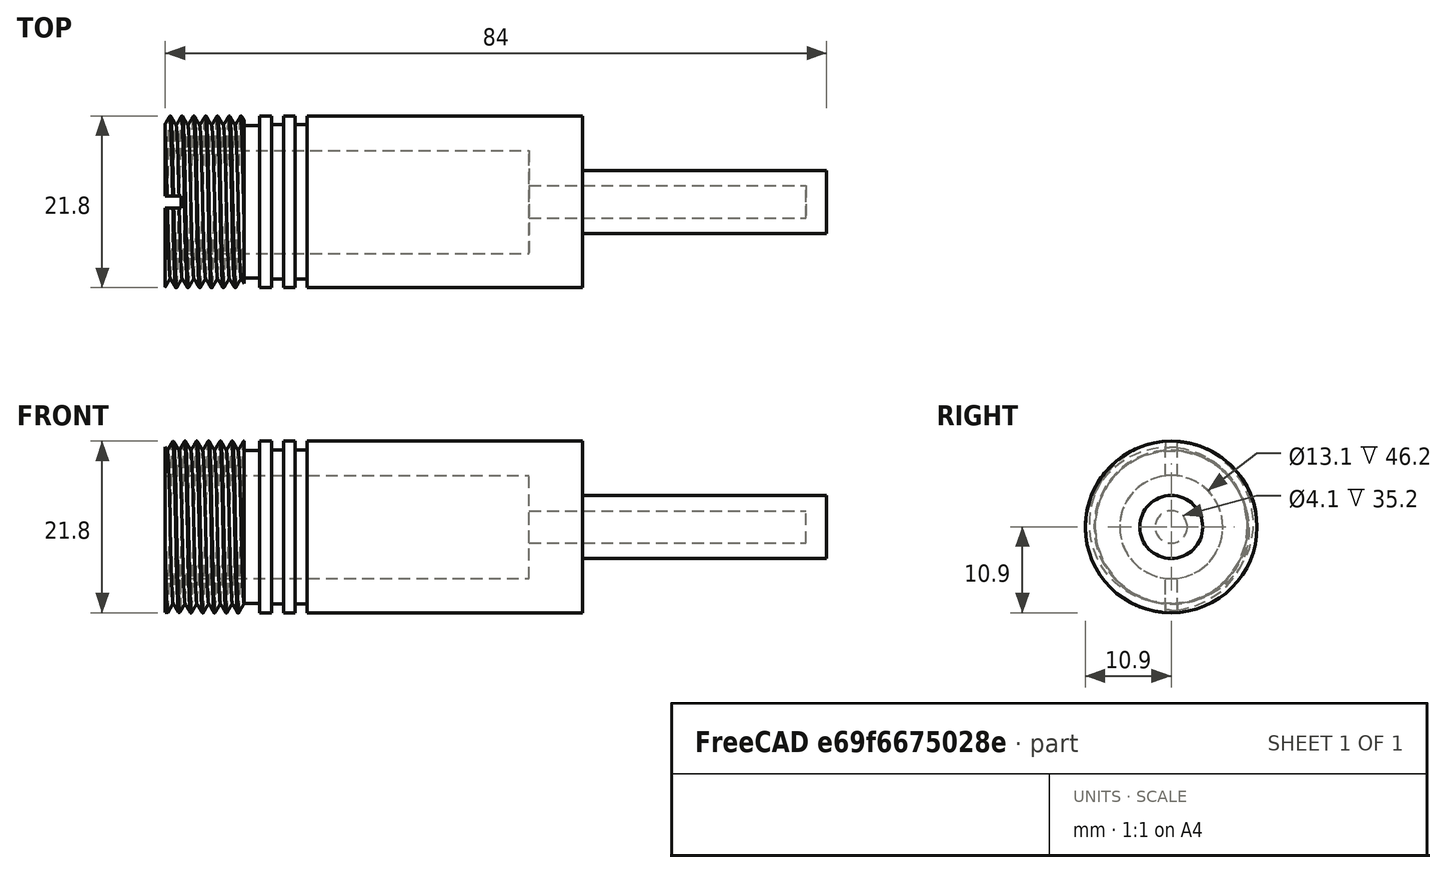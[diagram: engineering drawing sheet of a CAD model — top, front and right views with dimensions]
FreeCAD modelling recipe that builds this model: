
FCSTD DOCUMENT  (FreeCAD 0.17R13541 (Git))
Label: ERG-T-04-SH-01
License: All rights reserved
LicenseURL: http://en.wikipedia.org/wiki/All_rights_reserved
objects: Drawing::FeatureViewPython×17, Part::Cylinder×16, Part::Cut×11, Part::MultiFuse×4, Part::Helix×1, Sketcher::SketchObject×1, Part::Sweep×1, Part::Box×1, Drawing::FeatureViewPart×1, Drawing::FeaturePage×1
note: 35 computed .brp shape members not serialized (recipe doc carries the construction recipe); baked Part::Feature solids carry a one-line shape summary decoded from their .brp

FEATURE [Part::Cylinder] Cylinder072  label="Cylinder077"
  Angle = 360
  AttacherType = Attacher::AttachEngine3D
  Height = 18
  Placement = pos=(180.5,0,0) rot=(0,1,0;1.5708rad)
  Radius = 10.9
FEATURE [Part::Cylinder] Cylinder074  label="Cylinder083"
  Angle = 360
  AttacherType = Attacher::AttachEngine3D
  Height = 46.2
  Placement = pos=(180.5,0,0) rot=(0,1,0;1.5708rad)
  Radius = 6.55
FEATURE [Part::Cylinder] Cylinder075  label="Cylinder084"
  Angle = 360
  AttacherType = Attacher::AttachEngine3D
  Height = 53
  Placement = pos=(180.5,0,0) rot=(0,1,0;1.5708rad)
  Radius = 12.5
FEATURE [Part::Cylinder] Cylinder076  label="Cylinder085"
  Angle = 360
  AttacherType = Attacher::AttachEngine3D
  Height = 18
  Placement = pos=(180.5,0,0) rot=(0,1,0;1.5708rad)
  Radius = 12.5
FEATURE [Part::Cylinder] Cylinder077  label="Cylinder086"
  Angle = 360
  AttacherType = Attacher::AttachEngine3D
  Height = 31
  Placement = pos=(233.5,0,0) rot=(0,1,0;1.5708rad)
  Radius = 4
FEATURE [Part::Cut] Cut065
  Base = -> Cylinder076
  Tool = -> Cylinder072
FEATURE [Part::Cylinder] Cylinder080  label="Cylinder089"
  Angle = 360
  AttacherType = Attacher::AttachEngine3D
  Height = 35.2
  Placement = pos=(226.7,0,0) rot=(0,1,0;1.5708rad)
  Radius = 2.05
FEATURE [Part::MultiFuse] Fusion017  label="cavity"
  Shapes = -> [Cylinder080,Cylinder074]
FEATURE [Part::Helix] Helix019
  Angle = 0
  AttacherType = Attacher::AttachEngine3D
  Height = 17
  LocalCoord = 0
  Pitch = 1.5
  Placement = pos=(157,0,0) rot=(0,1,0;1.5708rad)
  Radius = 10.5
  Style = 1
FEATURE [Sketcher::SketchObject] Sketch023  label="T022"
  Placement = pos=(157,0,-11.01) rot=(1,0,0;1.5708rad)
  sketch-geometry (3):
    g0: LineSegment StartX=0 StartY=1.29904 StartZ=0 EndX=-0.75 EndY=0 EndZ=0
    g1: LineSegment StartX=0.75 StartY=0 StartZ=0 EndX=0 EndY=1.29904 EndZ=0
    g2: LineSegment StartX=-0.75 StartY=0 StartZ=0 EndX=0.75 EndY=0 EndZ=0
  constraints (9):
    c: PointOnObject(g1,g-1)
    c: Coincident(g1,g0)
    c: Coincident(g2,g0)
    c: Coincident(g2,g1)
    c: Horizontal(g2)
    c: Symmetric(g0,g1,g-2)
    c: Distance(g0,g1) = 1.5
    c: Angle(g1,g2) = 1.0472
    c: Angle(g2,g0) = 1.0472
FEATURE [Part::Sweep] Sweep016
  Frenet = true
  Sections = -> [Sketch023]
  Solid = true
  Spine = -> Helix019
  Transition = 1
FEATURE [Part::Cylinder] Cylinder084  label="Cylinder092"
  Angle = 360
  AttacherType = Attacher::AttachEngine3D
  Height = 1.5
  Placement = pos=(178,0,0) rot=(0,1,0;1.5708rad)
  Radius = 11
FEATURE [Part::Cylinder] Cylinder085  label="Cylinder093"
  Angle = 360
  AttacherType = Attacher::AttachEngine3D
  Height = 1.5
  Placement = pos=(178,0,0) rot=(0,1,0;1.5708rad)
  Radius = 9.8
FEATURE [Part::Cut] Cut071  label="circ2"
  Base = -> Cylinder084
  Placement = pos=(16,0,0) rot=(0,0,1;0rad)
  Tool = -> Cylinder085
FEATURE [Part::Cylinder] Cylinder086  label="Cylinder094"
  Angle = 360
  AttacherType = Attacher::AttachEngine3D
  Height = 2
  Placement = pos=(178,0,0) rot=(0,1,0;1.5708rad)
  Radius = 11
FEATURE [Part::Cylinder] Cylinder087  label="Cylinder095"
  Angle = 360
  AttacherType = Attacher::AttachEngine3D
  Height = 2
  Placement = pos=(178,0,0) rot=(0,1,0;1.5708rad)
  Radius = 9.7
FEATURE [Part::Cut] Cut072  label="circ1"
  Base = -> Cylinder086
  Placement = pos=(12.5,0,0) rot=(0,0,1;0rad)
  Tool = -> Cylinder087
FEATURE [Part::Cylinder] Cylinder088  label="Cylinder096"
  Angle = 360
  AttacherType = Attacher::AttachEngine3D
  Height = 10
  Placement = pos=(178,0,0) rot=(0,1,0;1.5708rad)
  Radius = 9
FEATURE [Part::Cylinder] Cylinder089  label="Cylinder097"
  Angle = 360
  AttacherType = Attacher::AttachEngine3D
  Height = 10
  Placement = pos=(178,0,0) rot=(0,1,0;1.5708rad)
  Radius = 11.5
FEATURE [Part::Cut] Cut074
  Base = -> Cylinder089
  Placement = pos=(-10.5,0,0) rot=(0,0,1;0rad)
  Tool = -> Cylinder088
FEATURE [Part::Box] Box  label="Cube"
  AttacherType = Attacher::AttachEngine3D
  Height = 30
  Length = 2
  Placement = pos=(180.5,-0.75,-15) rot=(0,0,1;0rad)
  Width = 1.5
FEATURE [Part::Cylinder] Cylinder091  label="Cylinder099"
  Angle = 360
  AttacherType = Attacher::AttachEngine3D
  Height = 35
  Placement = pos=(198.5,0,0) rot=(0,1,0;1.5708rad)
  Radius = 12.5
FEATURE [Part::Cylinder] Cylinder092  label="Cylinder100"
  Angle = 360
  AttacherType = Attacher::AttachEngine3D
  Height = 35
  Placement = pos=(198.5,0,0) rot=(0,1,0;1.5708rad)
  Radius = 10.9
FEATURE [Part::Cut] Cut
  Base = -> Cylinder091
  Tool = -> Cylinder092
FEATURE [Part::Cylinder] Cylinder093  label="Cylinder101"
  Angle = 360
  AttacherType = Attacher::AttachEngine3D
  Height = 1.5
  Placement = pos=(178,0,0) rot=(0,1,0;1.5708rad)
  Radius = 11
FEATURE [Part::Cylinder] Cylinder094  label="Cylinder102"
  Angle = 360
  AttacherType = Attacher::AttachEngine3D
  Height = 1.5
  Placement = pos=(178,0,0) rot=(0,1,0;1.5708rad)
  Radius = 9.8
FEATURE [Part::Cut] Cut076  label="circ3"
  Base = -> Cylinder093
  Placement = pos=(19,0,0) rot=(0,0,1;0rad)
  Tool = -> Cylinder094
FEATURE [Part::MultiFuse] Fusion019
  Shapes = -> [Cut,Cut065]
FEATURE [Part::MultiFuse] Fusion020
  Shapes = -> [Cylinder075,Cylinder077]
FEATURE [Part::Cut] Cut077  label="body"
  Base = -> Fusion020
  Tool = -> Fusion019
FEATURE [Part::Cut] Cut078  label="thread"
  Base = -> Sweep016
  Placement = pos=(23,0,0) rot=(0,0,1;0rad)
  Tool = -> Cut074
FEATURE [Part::MultiFuse] Fusion021  label="cutstuff"
  Shapes = -> [Cut078,Cut076,Cut072,Cut071]
FEATURE [Part::Cut] Cut079  label="outside"
  Base = -> Cut077
  Tool = -> Fusion021
FEATURE [Part::Cut] Cut080  label="holder01"
  Base = -> Cut079
  Tool = -> Fusion017
FEATURE [Part::Cut] Cut081  label="HOLDER"
  Base = -> Cut080
  Tool = -> Box
FEATURE [Drawing::FeatureViewPart] Ortho  label="Ortho_0_0"
  Direction = (0,1,0)
  HiddenWidth = 0.15
  LineWidth = 0.35
  Rotation = 90
  Scale = 2.5
  ShowHiddenLines = true
  ShowSmoothLines = false
  Source = -> Cut081
  Tolerance = 0.05
  ViewResult = <blob: 32848 chars omitted>
  Visible = true
  X = -407.75
  Y = 73.1186
FEATURE [Drawing::FeatureViewPython] dim001  # drawing view (typed FeaturePython)
  Rotation = 0
  ViewResult = <g> \n  <line x1="247.000000" y1="67.993600" x2="243.013684" y2="67.993600" style="stroke:rgb(255,0,0);stroke-width:0.10" />\n<line x1="247.000000" y1="78.243600" x2="243.013684" y2="78.243600" style="stroke:rgb(255,0,0);stroke-width:0.10" />\n<line x1="244.013684" y1="67.993600" x2="244.013684" y2="78.243600" style="stroke:rgb(255,0,0);stroke-width:0.10" /> \n  <polygon points="244.013684,78.243600 244.513684,76.243600 244.013684,75.743600 243.513684,76.243600" style="fill:rgb(255,0,0);stroke:rgb(255,0,0);stroke-width:0" /><polygon points="244.013684,67.993600 243.513684,69.993600 244.013684,70.493600 244.513684,69.993600" style="fill:rgb(255,0,0);stroke:rgb(255,0,0);stroke-width:0" /> \n  <text x="242.013684" y="73.118600" font-family="inherit" font-size="3.6" fill="rgb(0,0,0)" text-anchor="middle" transform="rotate(-90.000000 242.013684,73.118600)" >4.1</text> </g>
  Visible = true
  X = 0
  Y = 0
  arrowL1 = 2
  arrowL2 = 0.5
  arrowW = 1
  arrow_scheme = 0
  autoPlaceOffset = 2
  autoPlaceText = true
  click1_x = 244.014
  click1_y = 78.2593
  click2_x = 244.014
  click2_y = 78.2593
  comma_decimal_place = false
  dimension_line_overshoot = 1
  gap_datum_points = 0
  halfDimension_linear = false
  lineColor = rgb(255,0,0)
  strokeWidth = 0.1
  textFormat_linear = %(value)3.3f
  textRenderer_color = rgb(0,0,0)
  textRenderer_family = inherit
  textRenderer_size = 3.6
  unit_custom_scale = 1
  unit_scheme = 0
FEATURE [Drawing::FeatureViewPython] dim002  # drawing view (typed FeaturePython)
  Rotation = 0
  ViewResult = <g> \n  <line x1="253.500000" y1="63.118600" x2="263.329431" y2="63.118600" style="stroke:rgb(255,0,0);stroke-width:0.10" />\n<line x1="253.500000" y1="83.118600" x2="263.329431" y2="83.118600" style="stroke:rgb(255,0,0);stroke-width:0.10" />\n<line x1="262.329431" y1="63.118600" x2="262.329431" y2="83.118600" style="stroke:rgb(255,0,0);stroke-width:0.10" /> \n  <polygon points="262.329431,83.118600 262.829431,81.118600 262.329431,80.618600 261.829431,81.118600" style="fill:rgb(255,0,0);stroke:rgb(255,0,0);stroke-width:0" /><polygon points="262.329431,63.118600 261.829431,65.118600 262.329431,65.618600 262.829431,65.118600" style="fill:rgb(255,0,0);stroke:rgb(255,0,0);stroke-width:0" /> \n  <text x="260.329431" y="73.118600" font-family="inherit" font-size="3.6" fill="rgb(0,0,0)" text-anchor="middle" transform="rotate(-90.000000 260.329431,73.118600)" >8</text> </g>
  Visible = true
  X = 0
  Y = 0
  arrowL1 = 2
  arrowL2 = 0.5
  arrowW = 1
  arrow_scheme = 0
  autoPlaceOffset = 2
  autoPlaceText = true
  click1_x = 262.329
  click1_y = 85.3497
  click2_x = 262.329
  click2_y = 85.3497
  comma_decimal_place = false
  dimension_line_overshoot = 1
  gap_datum_points = 0
  halfDimension_linear = false
  lineColor = rgb(255,0,0)
  strokeWidth = 0.1
  textFormat_linear = %(value)3.3f
  textRenderer_color = rgb(0,0,0)
  textRenderer_family = inherit
  textRenderer_size = 3.6
  unit_custom_scale = 1
  unit_scheme = 0
FEATURE [Drawing::FeatureViewPython] dim005  # drawing view (typed FeaturePython)
  Rotation = 0
  ViewResult = <g> \n  <line x1="88.500000" y1="45.868600" x2="88.500000" y2="32.082769" style="stroke:rgb(255,0,0);stroke-width:0.10" />\n<line x1="176.000000" y1="45.868600" x2="176.000000" y2="32.082769" style="stroke:rgb(255,0,0);stroke-width:0.10" />\n<line x1="88.500000" y1="33.082769" x2="176.000000" y2="33.082769" style="stroke:rgb(255,0,0);stroke-width:0.10" /> \n  <polygon points="176.000000,33.082769 174.000000,32.582769 173.500000,33.082769 174.000000,33.582769" style="fill:rgb(255,0,0);stroke:rgb(255,0,0);stroke-width:0" /><polygon points="88.500000,33.082769 90.500000,33.582769 91.000000,33.082769 90.500000,32.582769" style="fill:rgb(255,0,0);stroke:rgb(255,0,0);stroke-width:0" /> \n  <text x="132.250000" y="31.082769" font-family="inherit" font-size="3.6" fill="rgb(0,0,0)" text-anchor="middle" transform="rotate(0.000000 132.250000,31.082769)" >35</text> </g>
  Visible = true
  X = 0
  Y = 0
  arrowL1 = 2
  arrowL2 = 0.5
  arrowW = 1
  arrow_scheme = 0
  autoPlaceOffset = 2
  autoPlaceText = true
  click1_x = 161.182
  click1_y = 33.0828
  click2_x = 161.182
  click2_y = 33.0828
  comma_decimal_place = false
  dimension_line_overshoot = 1
  gap_datum_points = 0
  halfDimension_linear = false
  lineColor = rgb(255,0,0)
  strokeWidth = 0.1
  textFormat_linear = %(value)3.3f
  textRenderer_color = rgb(0,0,0)
  textRenderer_family = inherit
  textRenderer_size = 3.6
  unit_custom_scale = 1
  unit_scheme = 0
FEATURE [Drawing::FeatureViewPython] dim006  # drawing view (typed FeaturePython)
  Rotation = 0
  ViewResult = <g> \n  <line x1="88.500000" y1="45.868600" x2="88.500000" y2="32.094010" style="stroke:rgb(255,0,0);stroke-width:0.10" />\n<line x1="68.500000" y1="48.819225" x2="68.500000" y2="32.094010" style="stroke:rgb(255,0,0);stroke-width:0.10" />\n<line x1="88.500000" y1="33.094010" x2="68.500000" y2="33.094010" style="stroke:rgb(255,0,0);stroke-width:0.10" /> \n  <polygon points="68.500000,33.094010 70.500000,33.594010 71.000000,33.094010 70.500000,32.594010" style="fill:rgb(255,0,0);stroke:rgb(255,0,0);stroke-width:0" /><polygon points="88.500000,33.094010 86.500000,32.594010 86.000000,33.094010 86.500000,33.594010" style="fill:rgb(255,0,0);stroke:rgb(255,0,0);stroke-width:0" /> \n  <text x="78.500000" y="31.094010" font-family="inherit" font-size="3.6" fill="rgb(0,0,0)" text-anchor="middle" transform="rotate(0.000000 78.500000,31.094010)" >8</text> </g>
  Visible = true
  X = 0
  Y = 0
  arrowL1 = 2
  arrowL2 = 0.5
  arrowW = 1
  arrow_scheme = 0
  autoPlaceOffset = 2
  autoPlaceText = true
  click1_x = 69.9279
  click1_y = 33.094
  click2_x = 69.9279
  click2_y = 33.094
  comma_decimal_place = false
  dimension_line_overshoot = 1
  gap_datum_points = 0
  halfDimension_linear = false
  lineColor = rgb(255,0,0)
  strokeWidth = 0.1
  textFormat_linear = %(value)3.3f
  textRenderer_color = rgb(0,0,0)
  textRenderer_family = inherit
  textRenderer_size = 3.6
  unit_custom_scale = 1
  unit_scheme = 0
FEATURE [Drawing::FeatureViewPython] dim007  # drawing view (typed FeaturePython)
  Rotation = 0
  ViewResult = <g> \n  <line x1="68.500000" y1="48.819225" x2="68.500000" y2="32.164573" style="stroke:rgb(255,0,0);stroke-width:0.10" />\n<line x1="43.500000" y1="45.933100" x2="43.500000" y2="32.164573" style="stroke:rgb(255,0,0);stroke-width:0.10" />\n<line x1="68.500000" y1="33.164573" x2="43.500000" y2="33.164573" style="stroke:rgb(255,0,0);stroke-width:0.10" /> \n  <polygon points="43.500000,33.164573 45.500000,33.664573 46.000000,33.164573 45.500000,32.664573" style="fill:rgb(255,0,0);stroke:rgb(255,0,0);stroke-width:0" /><polygon points="68.500000,33.164573 66.500000,32.664573 66.000000,33.164573 66.500000,33.664573" style="fill:rgb(255,0,0);stroke:rgb(255,0,0);stroke-width:0" /> \n  <text x="56.000000" y="31.164573" font-family="inherit" font-size="3.6" fill="rgb(0,0,0)" text-anchor="middle" transform="rotate(0.000000 56.000000,31.164573)" >10</text> </g>
  Visible = true
  X = 0
  Y = 0
  arrowL1 = 2
  arrowL2 = 0.5
  arrowW = 1
  arrow_scheme = 0
  autoPlaceOffset = 2
  autoPlaceText = true
  click1_x = 44.5958
  click1_y = 33.1646
  click2_x = 44.5958
  click2_y = 33.1646
  comma_decimal_place = false
  dimension_line_overshoot = 1
  gap_datum_points = 0
  halfDimension_linear = false
  lineColor = rgb(255,0,0)
  strokeWidth = 0.1
  textFormat_linear = %(value)3.3f
  textRenderer_color = rgb(0,0,0)
  textRenderer_family = inherit
  textRenderer_size = 3.6
  unit_custom_scale = 1
  unit_scheme = 0
FEATURE [Drawing::FeatureViewPython] dim004  # drawing view (typed FeaturePython)
  Rotation = 0
  ViewResult = <g> \n  <line x1="176.000000" y1="63.118600" x2="176.000000" y2="32.081558" style="stroke:rgb(255,0,0);stroke-width:0.10" />\n<line x1="253.500000" y1="63.118600" x2="253.500000" y2="32.081558" style="stroke:rgb(255,0,0);stroke-width:0.10" />\n<line x1="176.000000" y1="33.081558" x2="253.500000" y2="33.081558" style="stroke:rgb(255,0,0);stroke-width:0.10" /> \n  <polygon points="253.500000,33.081558 251.500000,32.581558 251.000000,33.081558 251.500000,33.581558" style="fill:rgb(255,0,0);stroke:rgb(255,0,0);stroke-width:0" /><polygon points="176.000000,33.081558 178.000000,33.581558 178.500000,33.081558 178.000000,32.581558" style="fill:rgb(255,0,0);stroke:rgb(255,0,0);stroke-width:0" /> \n  <text x="214.750000" y="31.081558" font-family="inherit" font-size="3.6" fill="rgb(0,0,0)" text-anchor="middle" transform="rotate(0.000000 214.750000,31.081558)" >31</text> </g>
  Visible = true
  X = 0
  Y = 0
  arrowL1 = 2
  arrowL2 = 0.5
  arrowW = 1
  arrow_scheme = 0
  autoPlaceOffset = 2
  autoPlaceText = true
  click1_x = 187.265
  click1_y = 33.0816
  click2_x = 187.265
  click2_y = 33.0816
  comma_decimal_place = false
  dimension_line_overshoot = 1
  gap_datum_points = 0
  halfDimension_linear = false
  lineColor = rgb(255,0,0)
  strokeWidth = 0.1
  textFormat_linear = %(value)3.3f
  textRenderer_color = rgb(0,0,0)
  textRenderer_family = inherit
  textRenderer_size = 3.6
  unit_custom_scale = 1
  unit_scheme = 0
FEATURE [Drawing::FeatureViewPython] dim008  # drawing view (typed FeaturePython)
  Rotation = 0
  ViewResult = <g> \n  <line x1="159.000000" y1="56.743600" x2="150.188443" y2="56.743600" style="stroke:rgb(255,0,0);stroke-width:0.10" />\n<line x1="159.000000" y1="89.493600" x2="150.188443" y2="89.493600" style="stroke:rgb(255,0,0);stroke-width:0.10" />\n<line x1="151.188443" y1="56.743600" x2="151.188443" y2="89.493600" style="stroke:rgb(255,0,0);stroke-width:0.10" /> \n  <polygon points="151.188443,89.493600 151.688443,87.493600 151.188443,86.993600 150.688443,87.493600" style="fill:rgb(255,0,0);stroke:rgb(255,0,0);stroke-width:0" /><polygon points="151.188443,56.743600 150.688443,58.743600 151.188443,59.243600 151.688443,58.743600" style="fill:rgb(255,0,0);stroke:rgb(255,0,0);stroke-width:0" /> \n  <text x="149.188443" y="73.118600" font-family="inherit" font-size="3.6" fill="rgb(0,0,0)" text-anchor="middle" transform="rotate(-90.000000 149.188443,73.118600)" >13.1</text> </g>
  Visible = true
  X = 0
  Y = 0
  arrowL1 = 2
  arrowL2 = 0.5
  arrowW = 1
  arrow_scheme = 0
  autoPlaceOffset = 2
  autoPlaceText = true
  click1_x = 151.188
  click1_y = 89.0644
  click2_x = 151.188
  click2_y = 89.0644
  comma_decimal_place = false
  dimension_line_overshoot = 1
  gap_datum_points = 0
  halfDimension_linear = false
  lineColor = rgb(255,0,0)
  strokeWidth = 0.1
  textFormat_linear = %(value)3.3f
  textRenderer_color = rgb(0,0,0)
  textRenderer_family = inherit
  textRenderer_size = 3.6
  unit_custom_scale = 1
  unit_scheme = 0
FEATURE [Drawing::FeatureViewPython] dim009  # drawing view (typed FeaturePython)
  Rotation = 0
  ViewResult = <g> \n  <line x1="43.500000" y1="45.933100" x2="43.500000" y2="19.353229" style="stroke:rgb(255,0,0);stroke-width:0.10" />\n<line x1="253.500000" y1="63.118600" x2="253.500000" y2="19.353229" style="stroke:rgb(255,0,0);stroke-width:0.10" />\n<line x1="43.500000" y1="20.353229" x2="253.500000" y2="20.353229" style="stroke:rgb(255,0,0);stroke-width:0.10" /> \n  <polygon points="253.500000,20.353229 251.500000,19.853229 251.000000,20.353229 251.500000,20.853229" style="fill:rgb(255,0,0);stroke:rgb(255,0,0);stroke-width:0" /><polygon points="43.500000,20.353229 45.500000,20.853229 46.000000,20.353229 45.500000,19.853229" style="fill:rgb(255,0,0);stroke:rgb(255,0,0);stroke-width:0" /> \n  <text x="148.500000" y="18.353229" font-family="inherit" font-size="3.6" fill="rgb(0,0,0)" text-anchor="middle" transform="rotate(0.000000 148.500000,18.353229)" >84</text> </g>
  Visible = true
  X = 0
  Y = 0
  arrowL1 = 2
  arrowL2 = 0.5
  arrowW = 1
  arrow_scheme = 0
  autoPlaceOffset = 2
  autoPlaceText = true
  click1_x = 240.819
  click1_y = 20.3532
  click2_x = 240.819
  click2_y = 20.3532
  comma_decimal_place = false
  dimension_line_overshoot = 1
  gap_datum_points = 0
  halfDimension_linear = false
  lineColor = rgb(255,0,0)
  strokeWidth = 0.1
  textFormat_linear = %(value)3.3f
  textRenderer_color = rgb(0,0,0)
  textRenderer_family = inherit
  textRenderer_size = 3.6
  unit_custom_scale = 1
  unit_scheme = 0
FEATURE [Drawing::FeatureViewPython] dim010  # drawing view (typed FeaturePython)
  Rotation = 0
  ViewResult = <g> \n  <line x1="247.000000" y1="78.243600" x2="247.000000" y2="113.371059" style="stroke:rgb(255,0,0);stroke-width:0.10" />\n<line x1="159.000000" y1="89.493600" x2="159.000000" y2="113.371059" style="stroke:rgb(255,0,0);stroke-width:0.10" />\n<line x1="247.000000" y1="112.371059" x2="159.000000" y2="112.371059" style="stroke:rgb(255,0,0);stroke-width:0.10" /> \n  <polygon points="159.000000,112.371059 161.000000,112.871059 161.500000,112.371059 161.000000,111.871059" style="fill:rgb(255,0,0);stroke:rgb(255,0,0);stroke-width:0" /><polygon points="247.000000,112.371059 245.000000,111.871059 244.500000,112.371059 245.000000,112.871059" style="fill:rgb(255,0,0);stroke:rgb(255,0,0);stroke-width:0" /> \n  <text x="203.000000" y="110.371059" font-family="inherit" font-size="3.6" fill="rgb(0,0,0)" text-anchor="middle" transform="rotate(0.000000 203.000000,110.371059)" >35.2</text> </g>
  Visible = true
  X = 0
  Y = 0
  arrowL1 = 2
  arrowL2 = 0.5
  arrowW = 1
  arrow_scheme = 0
  autoPlaceOffset = 2
  autoPlaceText = true
  click1_x = 170.192
  click1_y = 112.371
  click2_x = 170.192
  click2_y = 112.371
  comma_decimal_place = false
  dimension_line_overshoot = 1
  gap_datum_points = 0
  halfDimension_linear = false
  lineColor = rgb(255,0,0)
  strokeWidth = 0.1
  textFormat_linear = %(value)3.3f
  textRenderer_color = rgb(0,0,0)
  textRenderer_family = inherit
  textRenderer_size = 3.6
  unit_custom_scale = 1
  unit_scheme = 0
FEATURE [Drawing::FeatureViewPython] dim011  # drawing view (typed FeaturePython)
  Rotation = 0
  ViewResult = <g> \n  <line x1="159.000000" y1="89.493600" x2="159.000000" y2="113.377984" style="stroke:rgb(255,0,0);stroke-width:0.10" />\n<line x1="43.500000" y1="98.332100" x2="43.500000" y2="113.377984" style="stroke:rgb(255,0,0);stroke-width:0.10" />\n<line x1="159.000000" y1="112.377984" x2="43.500000" y2="112.377984" style="stroke:rgb(255,0,0);stroke-width:0.10" /> \n  <polygon points="43.500000,112.377984 45.500000,112.877984 46.000000,112.377984 45.500000,111.877984" style="fill:rgb(255,0,0);stroke:rgb(255,0,0);stroke-width:0" /><polygon points="159.000000,112.377984 157.000000,111.877984 156.500000,112.377984 157.000000,112.877984" style="fill:rgb(255,0,0);stroke:rgb(255,0,0);stroke-width:0" /> \n  <text x="101.250000" y="110.377984" font-family="inherit" font-size="3.6" fill="rgb(0,0,0)" text-anchor="middle" transform="rotate(0.000000 101.250000,110.377984)" >46.2</text> </g>
  Visible = true
  X = 0
  Y = 0
  arrowL1 = 2
  arrowL2 = 0.5
  arrowW = 1
  arrow_scheme = 0
  autoPlaceOffset = 2
  autoPlaceText = true
  click1_x = 155.5
  click1_y = 112.378
  click2_x = 155.5
  click2_y = 112.378
  comma_decimal_place = false
  dimension_line_overshoot = 1
  gap_datum_points = 0
  halfDimension_linear = false
  lineColor = rgb(255,0,0)
  strokeWidth = 0.1
  textFormat_linear = %(value)3.3f
  textRenderer_color = rgb(0,0,0)
  textRenderer_family = inherit
  textRenderer_size = 3.6
  unit_custom_scale = 1
  unit_scheme = 0
FEATURE [Drawing::FeatureViewPython] dim013  # drawing view (typed FeaturePython)
  Rotation = 0
  ViewResult = <g> \n  <line x1="88.500000" y1="48.618600" x2="96.671560" y2="48.618600" style="stroke:rgb(255,0,0);stroke-width:0.10" />\n<line x1="88.500000" y1="97.618600" x2="96.671560" y2="97.618600" style="stroke:rgb(255,0,0);stroke-width:0.10" />\n<line x1="95.671560" y1="48.618600" x2="95.671560" y2="97.618600" style="stroke:rgb(255,0,0);stroke-width:0.10" /> \n  <polygon points="95.671560,97.618600 96.171560,95.618600 95.671560,95.118600 95.171560,95.618600" style="fill:rgb(255,0,0);stroke:rgb(255,0,0);stroke-width:0" /><polygon points="95.671560,48.618600 95.171560,50.618600 95.671560,51.118600 96.171560,50.618600" style="fill:rgb(255,0,0);stroke:rgb(255,0,0);stroke-width:0" /> \n  <text x="93.671560" y="73.118600" font-family="inherit" font-size="3.6" fill="rgb(0,0,0)" text-anchor="middle" transform="rotate(-90.000000 93.671560,73.118600)" >19.6</text> </g>
  Visible = true
  X = 0
  Y = 0
  arrowL1 = 2
  arrowL2 = 0.5
  arrowW = 1
  arrow_scheme = 0
  autoPlaceOffset = 2
  autoPlaceText = true
  click1_x = 95.6716
  click1_y = 97.5532
  click2_x = 95.6716
  click2_y = 97.5532
  comma_decimal_place = false
  dimension_line_overshoot = 1
  gap_datum_points = 0
  halfDimension_linear = false
  lineColor = rgb(255,0,0)
  strokeWidth = 0.1
  textFormat_linear = %(value)3.3f
  textRenderer_color = rgb(0,0,0)
  textRenderer_family = inherit
  textRenderer_size = 3.6
  unit_custom_scale = 1
  unit_scheme = 0
FEATURE [Drawing::FeatureViewPython] dim003  # drawing view (typed FeaturePython)
  Rotation = 0
  ViewResult = <g> \n  <line x1="84.750000" y1="45.868600" x2="106.065366" y2="45.868600" style="stroke:rgb(255,0,0);stroke-width:0.10" />\n<line x1="84.750000" y1="100.368600" x2="106.065366" y2="100.368600" style="stroke:rgb(255,0,0);stroke-width:0.10" />\n<line x1="105.065366" y1="45.868600" x2="105.065366" y2="100.368600" style="stroke:rgb(255,0,0);stroke-width:0.10" /> \n  <polygon points="105.065366,100.368600 105.565366,98.368600 105.065366,97.868600 104.565366,98.368600" style="fill:rgb(255,0,0);stroke:rgb(255,0,0);stroke-width:0" /><polygon points="105.065366,45.868600 104.565366,47.868600 105.065366,48.368600 105.565366,47.868600" style="fill:rgb(255,0,0);stroke:rgb(255,0,0);stroke-width:0" /> \n  <text x="103.065366" y="73.118600" font-family="inherit" font-size="3.6" fill="rgb(0,0,0)" text-anchor="middle" transform="rotate(-90.000000 103.065366,73.118600)" >21.8</text> </g>
  Visible = true
  X = 0
  Y = 0
  arrowL1 = 2
  arrowL2 = 0.5
  arrowW = 1
  arrow_scheme = 0
  autoPlaceOffset = 2
  autoPlaceText = true
  click1_x = 105.065
  click1_y = 100.188
  click2_x = 105.065
  click2_y = 100.188
  comma_decimal_place = false
  dimension_line_overshoot = 1
  gap_datum_points = 0
  halfDimension_linear = false
  lineColor = rgb(255,0,0)
  strokeWidth = 0.1
  textFormat_linear = %(value)3.3f
  textRenderer_color = rgb(0,0,0)
  textRenderer_family = inherit
  textRenderer_size = 3.6
  unit_custom_scale = 1
  unit_scheme = 0
FEATURE [Drawing::FeatureViewPython] dim012  # drawing view (typed FeaturePython)
  Rotation = 0
  ViewResult = <g> \n  <line x1="68.500000" y1="97.368600" x2="68.500000" y2="108.151101" style="stroke:rgb(255,0,0);stroke-width:0.10" />\n<line x1="73.500000" y1="97.368600" x2="73.500000" y2="108.151101" style="stroke:rgb(255,0,0);stroke-width:0.10" />\n<line x1="68.500000" y1="107.151101" x2="73.500000" y2="107.151101" style="stroke:rgb(255,0,0);stroke-width:0.10" /> \n  <polygon points="73.500000,107.151101 75.500000,107.651101 76.000000,107.151101 75.500000,106.651101" style="fill:rgb(255,0,0);stroke:rgb(255,0,0);stroke-width:0" /><polygon points="68.500000,107.151101 66.500000,106.651101 66.000000,107.151101 66.500000,107.651101" style="fill:rgb(255,0,0);stroke:rgb(255,0,0);stroke-width:0" /> \n  <text x="71.000000" y="105.151101" font-family="inherit" font-size="3.6" fill="rgb(0,0,0)" text-anchor="middle" transform="rotate(0.000000 71.000000,105.151101)" >2</text> </g>
  Visible = true
  X = 0
  Y = 0
  arrowL1 = 2
  arrowL2 = 0.5
  arrowW = 1
  arrow_scheme = 0
  autoPlaceOffset = 2
  autoPlaceText = true
  click1_x = 70.3179
  click1_y = 107.151
  click2_x = 70.3179
  click2_y = 107.151
  comma_decimal_place = false
  dimension_line_overshoot = 1
  gap_datum_points = 0
  halfDimension_linear = false
  lineColor = rgb(255,0,0)
  strokeWidth = 0.1
  textFormat_linear = %(value)3.3f
  textRenderer_color = rgb(0,0,0)
  textRenderer_family = inherit
  textRenderer_size = 3.6
  unit_custom_scale = 1
  unit_scheme = 0
FEATURE [Drawing::FeatureViewPython] dim014  # drawing view (typed FeaturePython)
  Rotation = 0
  ViewResult = <g> \n  <line x1="84.750000" y1="97.618600" x2="84.750000" y2="107.946926" style="stroke:rgb(255,0,0);stroke-width:0.10" />\n<line x1="88.500000" y1="97.618600" x2="88.500000" y2="107.946926" style="stroke:rgb(255,0,0);stroke-width:0.10" />\n<line x1="84.750000" y1="106.946926" x2="88.500000" y2="106.946926" style="stroke:rgb(255,0,0);stroke-width:0.10" /> \n  <polygon points="88.500000,106.946926 90.500000,107.446926 91.000000,106.946926 90.500000,106.446926" style="fill:rgb(255,0,0);stroke:rgb(255,0,0);stroke-width:0" /><polygon points="84.750000,106.946926 82.750000,106.446926 82.250000,106.946926 82.750000,107.446926" style="fill:rgb(255,0,0);stroke:rgb(255,0,0);stroke-width:0" /> \n  <text x="86.625000" y="104.946926" font-family="inherit" font-size="3.6" fill="rgb(0,0,0)" text-anchor="middle" transform="rotate(0.000000 86.625000,104.946926)" >1.5</text> </g>
  Visible = true
  X = 0
  Y = 0
  arrowL1 = 2
  arrowL2 = 0.5
  arrowW = 1
  arrow_scheme = 0
  autoPlaceOffset = 2
  autoPlaceText = true
  click1_x = 86.2027
  click1_y = 106.947
  click2_x = 86.2027
  click2_y = 106.947
  comma_decimal_place = false
  dimension_line_overshoot = 1
  gap_datum_points = 0
  halfDimension_linear = false
  lineColor = rgb(255,0,0)
  strokeWidth = 0.1
  textFormat_linear = %(value)3.3f
  textRenderer_color = rgb(0,0,0)
  textRenderer_family = inherit
  textRenderer_size = 3.6
  unit_custom_scale = 1
  unit_scheme = 0
FEATURE [Drawing::FeatureViewPython] dim015  # drawing view (typed FeaturePython)
  Rotation = 0
  ViewResult = <g> \n  <line x1="77.250000" y1="97.618600" x2="77.250000" y2="111.662913" style="stroke:rgb(255,0,0);stroke-width:0.10" />\n<line x1="81.000000" y1="97.618600" x2="81.000000" y2="111.662913" style="stroke:rgb(255,0,0);stroke-width:0.10" />\n<line x1="77.250000" y1="110.662913" x2="81.000000" y2="110.662913" style="stroke:rgb(255,0,0);stroke-width:0.10" /> \n  <polygon points="81.000000,110.662913 83.000000,111.162913 83.500000,110.662913 83.000000,110.162913" style="fill:rgb(255,0,0);stroke:rgb(255,0,0);stroke-width:0" /><polygon points="77.250000,110.662913 75.250000,110.162913 74.750000,110.662913 75.250000,111.162913" style="fill:rgb(255,0,0);stroke:rgb(255,0,0);stroke-width:0" /> \n  <text x="79.125000" y="108.662913" font-family="inherit" font-size="3.6" fill="rgb(0,0,0)" text-anchor="middle" transform="rotate(0.000000 79.125000,108.662913)" >1.5</text> </g>
  Visible = true
  X = 0
  Y = 0
  arrowL1 = 2
  arrowL2 = 0.5
  arrowW = 1
  arrow_scheme = 0
  autoPlaceOffset = 2
  autoPlaceText = true
  click1_x = 79.4241
  click1_y = 110.663
  click2_x = 79.4241
  click2_y = 110.663
  comma_decimal_place = false
  dimension_line_overshoot = 1
  gap_datum_points = 0
  halfDimension_linear = false
  lineColor = rgb(255,0,0)
  strokeWidth = 0.1
  textFormat_linear = %(value)3.3f
  textRenderer_color = rgb(0,0,0)
  textRenderer_family = inherit
  textRenderer_size = 3.6
  unit_custom_scale = 1
  unit_scheme = 0
FEATURE [Drawing::FeatureViewPython] dim016  # drawing view (typed FeaturePython)
  Rotation = 0
  ViewResult = <g> \n  <line x1="73.500000" y1="45.868600" x2="73.500000" y2="40.139748" style="stroke:rgb(255,0,0);stroke-width:0.10" />\n<line x1="77.250000" y1="45.868600" x2="77.250000" y2="40.139748" style="stroke:rgb(255,0,0);stroke-width:0.10" />\n<line x1="73.500000" y1="41.139748" x2="77.250000" y2="41.139748" style="stroke:rgb(255,0,0);stroke-width:0.10" /> \n  <polygon points="77.250000,41.139748 79.250000,41.639748 79.750000,41.139748 79.250000,40.639748" style="fill:rgb(255,0,0);stroke:rgb(255,0,0);stroke-width:0" /><polygon points="73.500000,41.139748 71.500000,40.639748 71.000000,41.139748 71.500000,41.639748" style="fill:rgb(255,0,0);stroke:rgb(255,0,0);stroke-width:0" /> \n  <text x="75.375000" y="39.139748" font-family="inherit" font-size="3.6" fill="rgb(0,0,0)" text-anchor="middle" transform="rotate(0.000000 75.375000,39.139748)" >1.5</text> </g>
  Visible = true
  X = 0
  Y = 0
  arrowL1 = 2
  arrowL2 = 0.5
  arrowW = 1
  arrow_scheme = 0
  autoPlaceOffset = 2
  autoPlaceText = true
  click1_x = 74.1317
  click1_y = 41.1397
  click2_x = 74.1317
  click2_y = 41.1397
  comma_decimal_place = false
  dimension_line_overshoot = 1
  gap_datum_points = 0
  halfDimension_linear = false
  lineColor = rgb(255,0,0)
  strokeWidth = 0.1
  textFormat_linear = %(value)3.3f
  textRenderer_color = rgb(0,0,0)
  textRenderer_family = inherit
  textRenderer_size = 3.6
  unit_custom_scale = 1
  unit_scheme = 0
FEATURE [Drawing::FeatureViewPython] dim017  # drawing view (typed FeaturePython)
  Rotation = 0
  ViewResult = <g> \n  <line x1="81.000000" y1="45.868600" x2="81.000000" y2="40.153925" style="stroke:rgb(255,0,0);stroke-width:0.10" />\n<line x1="84.750000" y1="45.868600" x2="84.750000" y2="40.153925" style="stroke:rgb(255,0,0);stroke-width:0.10" />\n<line x1="81.000000" y1="41.153925" x2="84.750000" y2="41.153925" style="stroke:rgb(255,0,0);stroke-width:0.10" /> \n  <polygon points="84.750000,41.153925 86.750000,41.653925 87.250000,41.153925 86.750000,40.653925" style="fill:rgb(255,0,0);stroke:rgb(255,0,0);stroke-width:0" /><polygon points="81.000000,41.153925 79.000000,40.653925 78.500000,41.153925 79.000000,41.653925" style="fill:rgb(255,0,0);stroke:rgb(255,0,0);stroke-width:0" /> \n  <text x="82.875000" y="39.153925" font-family="inherit" font-size="3.6" fill="rgb(0,0,0)" text-anchor="middle" transform="rotate(0.000000 82.875000,39.153925)" >1.5</text> </g>
  Visible = true
  X = 0
  Y = 0
  arrowL1 = 2
  arrowL2 = 0.5
  arrowW = 1
  arrow_scheme = 0
  autoPlaceOffset = 2
  autoPlaceText = true
  click1_x = 79.363
  click1_y = 41.1539
  click2_x = 79.363
  click2_y = 41.1539
  comma_decimal_place = false
  dimension_line_overshoot = 1
  gap_datum_points = 0
  halfDimension_linear = false
  lineColor = rgb(255,0,0)
  strokeWidth = 0.1
  textFormat_linear = %(value)3.3f
  textRenderer_color = rgb(0,0,0)
  textRenderer_family = inherit
  textRenderer_size = 3.6
  unit_custom_scale = 1
  unit_scheme = 0
FEATURE [Drawing::FeaturePage] Page
  EditableTexts = Dr.Zoidberg | 24.10.2019 | x2.5 | ERG-T-04 | Sensor Holder | 1 | 1
  Group = -> [Ortho,dim001,dim002,dim005,dim006,dim007,dim004,dim008,dim009,dim010,dim011,dim013,dim003,dim012,dim014,dim015,dim016,dim017]
  Template = <path>
note: 1 file-system path scrubbed to <path> (originals preserved in the JSON sidecar)
